# Revit family: Wall_Hung_Lavatory_Sink-Elkay- ELV2219SACTMC
name_source: partatom
category: Plumbing Fixtures
units: mm (PartAtom-declared; Revit-internal decimal feet)

## family parameters
Cut with Voids When Loaded = No
Host = Face
Maintain Annotation Orientation = No
OmniClass Number = 23.45.05.14.14
OmniClass Title = Sinks/Lavatories
Part Type = Normal
Room Calculation Point = No
Round Connector Dimension = Use Diameter
Shared = No

## types (1)
- ELV2219SACTMC (Wall Hung Lavatory Sink Kit)
    Approx. Shipping Weight (lbs) = 28
    Assembly Code = D2010300
    Back Splash Height = 2.5 "
    Bowl 1 Dimensions = 16 inch x 11 1/2 inch x 5 1/2 inch
    Bowl Depth = 5.5 "
    Bowl Length = 16 "
    Bowl Width = 11.5 "
    CWFU = 0
    Default Elevation = 48 "
    Depth of Sink = 10 "
    Description = Stainless Steel 22 inch x 19 inch x 5 1/2 inch Wall Hung Lavatory Sink  Kit w/Sensor Faucet + Thermostatic Mixing Valve
    Drain Location = Rear Center
    Drain Size = 1.5 "
    Faucet Hole Size = 1.13 "
    Flow Rate (GPM) = 1 GPM
    Gauge = 18
    HWFU = 0
    Installation Type = Wall Hung
    Length of Sink = 22 "
    Main Material = Finish-Elkay-Stainless Steel
    Manufacturer = Elkay Manufacturer Company
    Manufacturer Brand = Elkay (by Zurn Elkay Water Solutions)
    Model = ELV2219SACTMC
    No of Bowls = 1
    Outlet Connection Size (inch) = 1.5 "
    Product Documentation Link = https://www.elkayfiles.com
    Product Installation Sheet URL = https://www.elkayfiles.com
    Product Page URL = https://www.elkay.com
    Product Weight (lbs) = 27
    Product data URL = https://www.bimobject.com
    R for masking = 1.75 "
    Repair Parts URL = https://www.elkayfiles.com
    Sink Dimensions = 22 inch x 19 inch x 10 inch
    Spout Height = 11.63 "
    Spout Reach = 5.63 "
    URL = https://www.elkay.com
    WFU = 0
    Width of Sink = 19 "

## geometry (parser evidence)
native form markers: Sweep x13
no freeform markers — native parametric forms only
